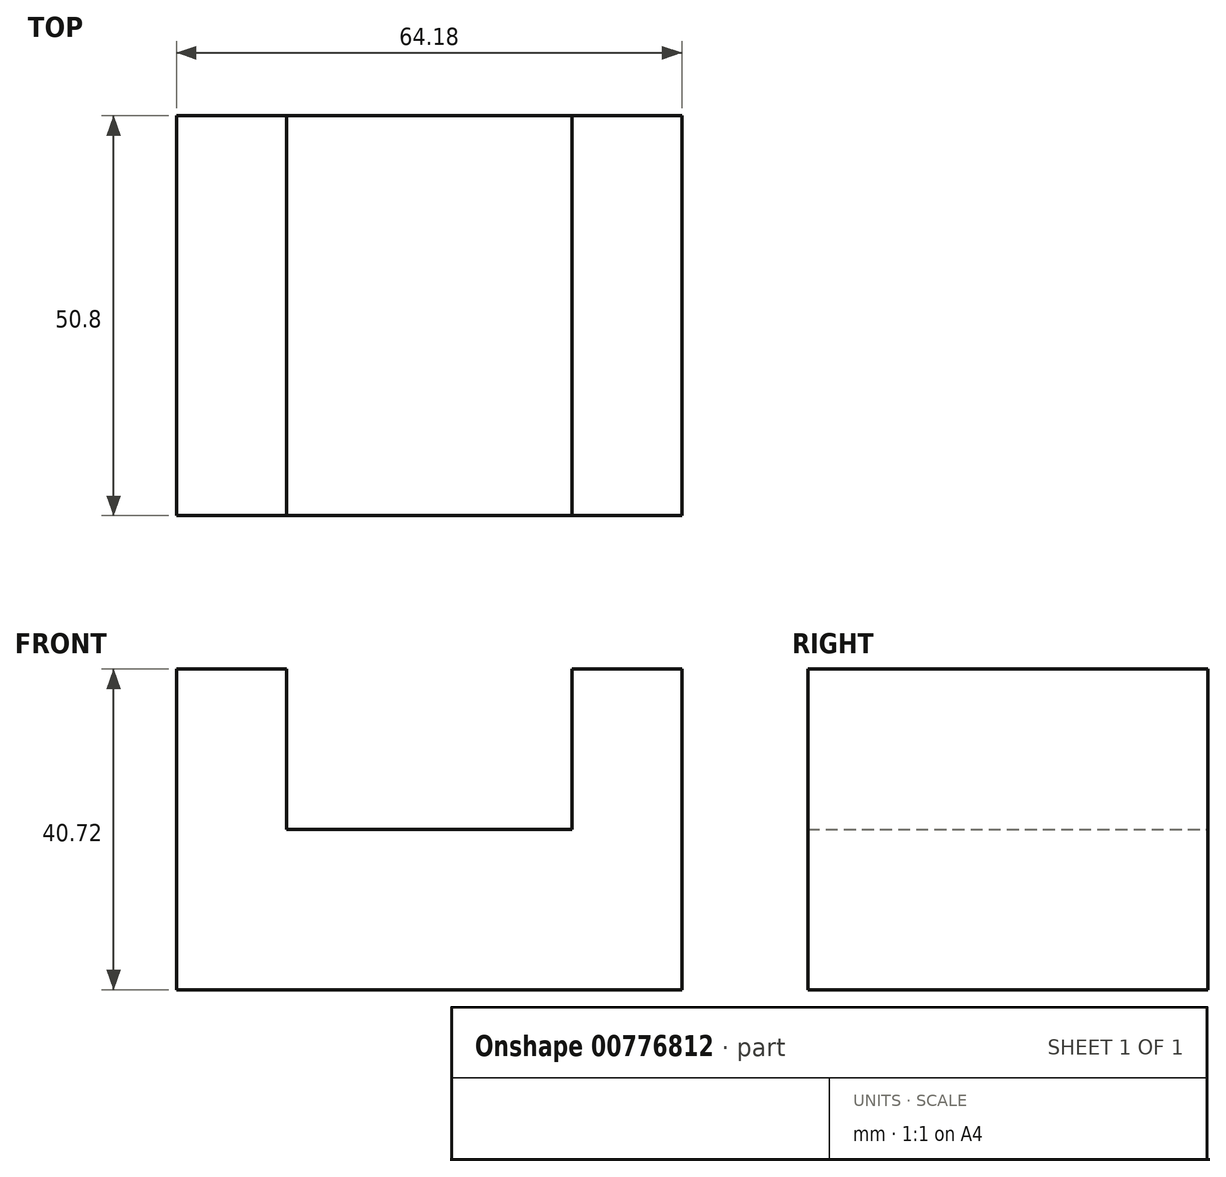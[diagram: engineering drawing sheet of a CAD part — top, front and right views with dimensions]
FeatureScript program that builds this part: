
annotation { "Feature Type Name" : "Feature", "Feature Type Description" : "" }
export const myFeature = defineFeature(function(context is Context, id is Id, definition is map)
    precondition{}
    {
        {
            var Q0;
            Q0=qCreatedBy(makeId("Front.planeOp"),FACE);
            var sketch = newSketch(context, id + "F0", { "sketchPlane" : qUnion([Q0])});
            skLineSegment(sketch, "E0.bottom", {"start": v(0, 0) * mm, "end": v(64.18, 0) * mm});
            skLineSegment(sketch, "E0.top", {"start": v(0, 40.72) * mm, "end": v(13.96, 40.72) * mm});
            skLineSegment(sketch, "E0.left", {"start": v(0, 0) * mm, "end": v(0, 40.72) * mm});
            skLineSegment(sketch, "E0.right", {"start": v(64.18, 0) * mm, "end": v(64.18, 40.72) * mm});
            skPoint(sketch, "E1.oppositeSnap0", {"position": v(0, 20.36) * mm});
            skLineSegment(sketch, "E1.top", {"start": v(13.96, 20.36) * mm, "end": v(50.22, 20.36) * mm});
            skLineSegment(sketch, "E1.left", {"start": v(13.96, 40.72) * mm, "end": v(13.96, 20.36) * mm});
            skLineSegment(sketch, "E1.right", {"start": v(50.22, 40.72) * mm, "end": v(50.22, 20.36) * mm});
            skLineSegment(sketch, "E2.trimOffspring", {"start": v(50.22, 40.72) * mm, "end": v(64.18, 40.72) * mm});
            skSolve(sketch);
        }
        {
            var Q0;
            Q0 = qSketchRegion(id + "F0", true);
            extrude(context, id + "F1", {"entities" : qUnion([Q0]), "depth" : 50.8 * mm, "offsetDistance" : 25.4 * mm});
        }
    });
